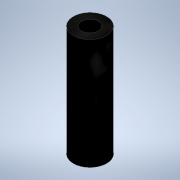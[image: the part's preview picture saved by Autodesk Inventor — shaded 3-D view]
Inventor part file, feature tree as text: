
AUTODESK INVENTOR PART (.ipt)
format: ipt  version: 2020.2 (Build 242310000, 310)  size: 91,648 bytes
history: native  units: mm
features: other x1, extrude x1, sketch x1
ambient origin geometry x8: Origin, YZ Plane, XZ Plane, XY Plane, X Axis, Y Axis, Z Axis, Center Point
bodies: Body1 (feature_tree)
feature tree (3):
  other  "ソリッド1"
  extrude  "押し出し1"  Depth=6.0mm
  sketch  "スケッチ1"
